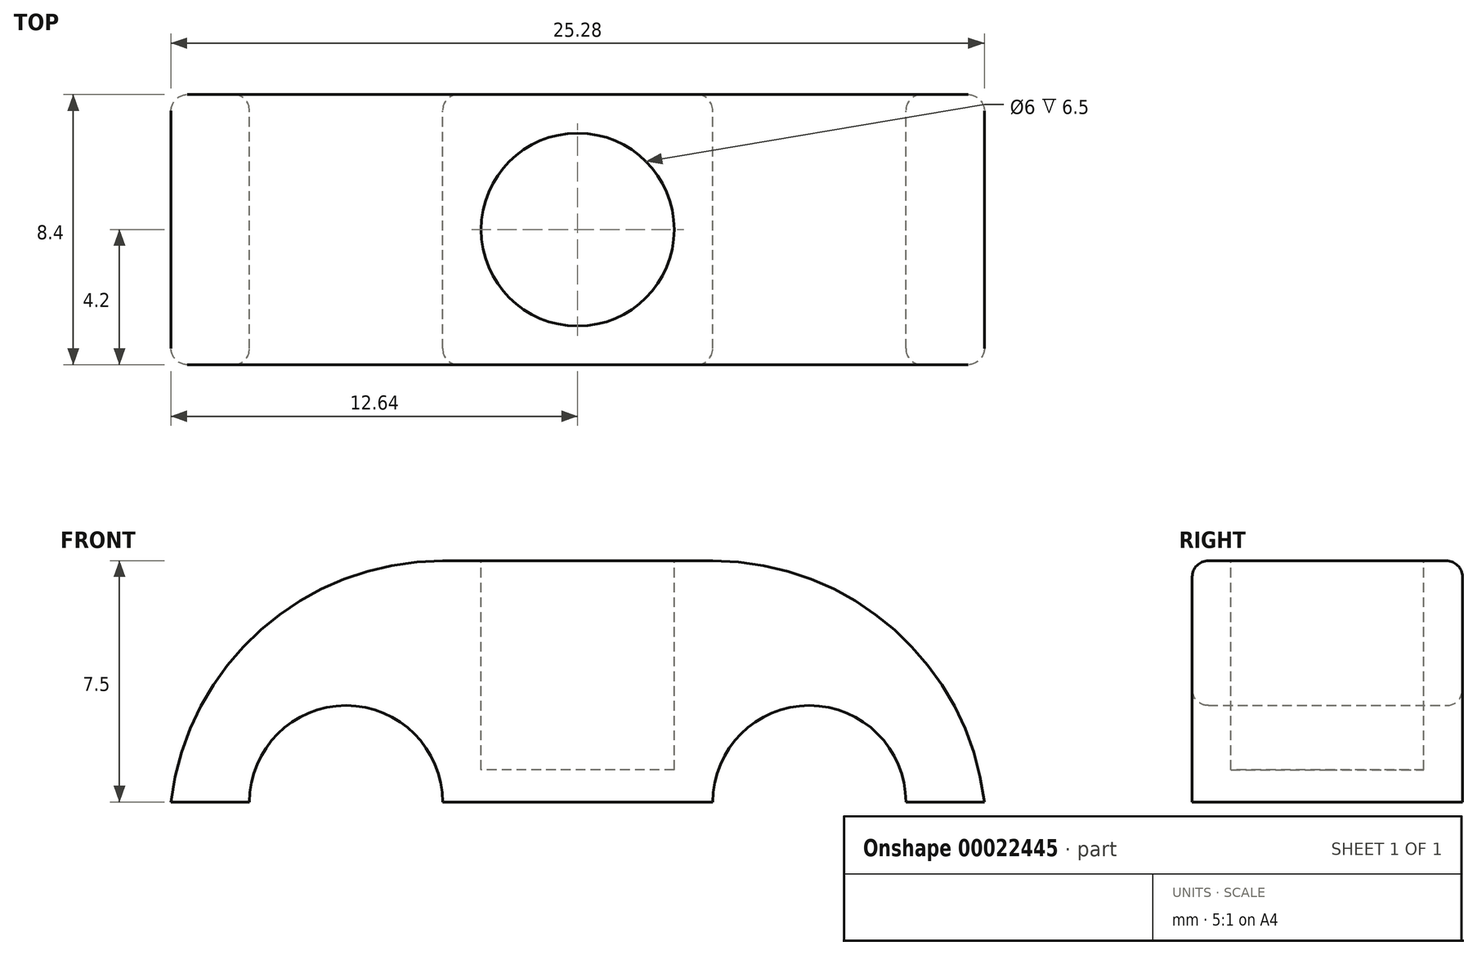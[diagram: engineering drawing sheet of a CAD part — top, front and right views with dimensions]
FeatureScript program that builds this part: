
annotation { "Feature Type Name" : "Feature", "Feature Type Description" : "" }
export const myFeature = defineFeature(function(context is Context, id is Id, definition is map)
    precondition{}
    {
        {
            var Q0;
            Q0=qCreatedBy(makeId("Front.planeOp"),FACE);
            var sketch = newSketch(context, id + "F0", { "sketchPlane" : qUnion([Q0])});
            skLineSegment(sketch, "E0.rect.bottom", {"start": v(3, 1) * mm, "end": v(-3, 1) * mm, "construction": true});
            skLineSegment(sketch, "E0.rect.top", {"start": v(3, 7) * mm, "end": v(-3, 7) * mm, "construction": true});
            skLineSegment(sketch, "E0.rect.left", {"start": v(3, 1) * mm, "end": v(3, 7) * mm, "construction": true});
            skLineSegment(sketch, "E0.rect.right", {"start": v(-3, 1) * mm, "end": v(-3, 7) * mm, "construction": true});
            skPoint(sketch, "E0.rect.middle", {"position": v(0, 4) * mm});
            skLineSegment(sketch, "E1.bottom", {"start": v(-4.2, 0) * mm, "end": v(4.2, 0) * mm});
            skLineSegment(sketch, "E1.top", {"start": v(-4.2, 7.5) * mm, "end": v(4.2, 7.5) * mm});
            skLineSegment(sketch, "E1.left", {"start": v(-4.2, 0) * mm, "end": v(-4.2, 7.5) * mm, "construction": true});
            skLineSegment(sketch, "E1.right", {"start": v(4.2, 0) * mm, "end": v(4.2, 7.5) * mm});
            skLineSegment(sketch, "E2", {"start": v(0, 7.5) * mm, "end": v(0, 0) * mm, "construction": true});
            skArc(sketch, "E3", {"start": v(-4.2, 0) * mm, "mid": v(-7.2, 3) * mm, "end": v(-10.2, 0) * mm});
            skArc(sketch, "E4", {"start": v(-4.2, 7.5) * mm, "mid": v(-9.85, 5.35) * mm, "end": v(-12.64, 0) * mm});
            skLineSegment(sketch, "E5", {"start": v(-12.64, 0) * mm, "end": v(-10.2, 0) * mm});
            skArc(sketch, "E6.MirrorCS", {"start": v(4.2, 7.5) * mm, "mid": v(9.85, 5.35) * mm, "end": v(12.64, 0) * mm});
            skLineSegment(sketch, "E7.MirrorCS", {"start": v(12.64, 0) * mm, "end": v(10.2, 0) * mm});
            skArc(sketch, "E8.MirrorCS", {"start": v(4.2, 0) * mm, "mid": v(7.2, 3) * mm, "end": v(10.2, 0) * mm});
            skSolve(sketch);
        }
        {
            var Q0;
            Q0 = qSketchRegion(id + "F0", true);
            extrude(context, id + "F1", {"entities" : qUnion([Q0]), "depth" : 8.4 * mm});
        }
        {
            var Q0;
            Q0=makeQuery(id+"F1.opExtrude","SWEPT_FACE",FACE,{"disambiguationData":[OSD([sQuery(id+"F0.wireOp",EDGE,"E1.top")])]});
            var sketch = newSketch(context, id + "F2", { "sketchPlane" : qUnion([Q0])});
            skCircle(sketch, "E9", {"center": v(0, -4.2) * mm, "radius": 3 * mm});
            skLineSegment(sketch, "E10", {"start": v(0, -8.4) * mm, "end": v(0, 0) * mm, "construction": true});
            skSolve(sketch);
        }
        {
            var Q0;
            Q0 = qSketchRegion(id + "F2", true);
            var Q1;
            Q1=makeQuery(id+"F1.opExtrude","SWEPT_FACE",FACE,{"disambiguationData":[OSD([sQuery(id+"F0.wireOp",EDGE,"E1.bottom")])]});
            extrude(context, id + "F3", {"entities" : qUnion([Q0]), "operationType" : NewBodyOperationType.REMOVE, "oppositeDirection" : true, "endBoundEntityFace" : qUnion([Q1]), "depth" : 6.5 * mm});
        }
        {
            var Q0;
            Q0=makeQuery(id+"F3.boolean.opBoolean","COPY",EDGE,{"derivedFrom":makeQuery(id+"F3.opExtrude","CAP_EDGE",EDGE,{"disambiguationData":[OSD([sQuery(id+"F2.wireOp",EDGE,"E9")])],"isStart":true})});
            var Q1;
            Q1=makeQuery(id+"F1.opExtrude","CAP_EDGE",EDGE,{"disambiguationData":[OSD([sQuery(id+"F0.wireOp",EDGE,"E4")])],"isStart":false});
            var Q2;
            Q2=makeQuery(id+"F1.opExtrude","CAP_EDGE",EDGE,{"disambiguationData":[OSD([sQuery(id+"F0.wireOp",EDGE,"E4")])],"isStart":true});
            var Q3;
            Q3=makeQuery(id+"F1.opExtrude","CAP_EDGE",EDGE,{"disambiguationData":[OSD([sQuery(id+"F0.wireOp",EDGE,"E1.top")])],"isStart":true});
            var Q4;
            Q4=makeQuery(id+"F1.opExtrude","CAP_EDGE",EDGE,{"disambiguationData":[OSD([sQuery(id+"F0.wireOp",EDGE,"E3")])],"isStart":false});
            var Q5;
            Q5=makeQuery(id+"F1.opExtrude","CAP_EDGE",EDGE,{"disambiguationData":[OSD([sQuery(id+"F0.wireOp",EDGE,"E8.MirrorCS")])],"isStart":false});
            var Q6;
            Q6=makeQuery(id+"F1.opExtrude","CAP_EDGE",EDGE,{"disambiguationData":[OSD([sQuery(id+"F0.wireOp",EDGE,"E8.MirrorCS")])],"isStart":true});
            var Q7;
            Q7=makeQuery(id+"F1.opExtrude","CAP_EDGE",EDGE,{"disambiguationData":[OSD([sQuery(id+"F0.wireOp",EDGE,"E3")])],"isStart":true});
            fillet(context, id + "F4", {"entities" : qUnion([Q0, Q1, Q2, Q3, Q4, Q5, Q6, Q7]), "radius" : .5 * mm, "tangentPropagation" : true, "allowEdgeOverflow" : false});
        }
    });
